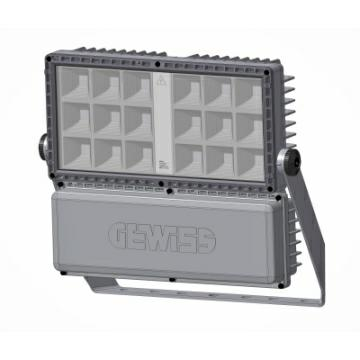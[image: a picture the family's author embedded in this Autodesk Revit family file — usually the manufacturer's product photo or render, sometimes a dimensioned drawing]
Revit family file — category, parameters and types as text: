
# Revit family: Lighting-Proiezione-GEWISS-SMART[PRO]2.0-PROIETTORI-LED-MEDIA-POTENZA_1MODULI_DALI_CLI
name_source: partatom
category: Apparecchi per illuminazione
units: mm (PartAtom-declared; Revit-internal decimal feet)

## family parameters
Condiviso = No
Host = Superficie
Punto di calcolo locali = Sì
Quota connettore circolare = Usa diametro
Sorgente d'illuminazione = No
Taglio con vuoti quando caricato = No
Tipo di parte = Normale

## types (1)
- Lighting-Proiezione-GEWISS-SMART[PRO]2.0-PROIETTORI-LED-MEDIA-POTENZA_1MODULI_DALI_CLI
    Alimentatore = Incluso
    Apparecchio a ridotta temperatura superficiale = Si
    Applicazione = Interno / Esterno
    Cablaggio = Connettore stagno
    Caratteristiche elettriche e gestione della luce = -
    Caratteristiche ottiche e illuminotecniche = -
    Catalogo = LIGHTING
    Certificazione DIN 18032-3 = Si
    Certificazioni e classificazioni = -
    Classe fotobiologica = -
    Classe isolamento = I
    Classificazione: = -
    Codice digitale univoco (Datamatrix) = Attualmente non presente
    Colore = Grigio grafite
    Contesto = Illuminazione di grandi aree, impianti sportivi
    Controllo abbagliamento e luminanza = G*6 - ULOR = 0
    Corpo = Alluminio pressofuso
    Descrizione = SMARTPRO2.0 1M 5700K CRI80 A3 DALI CL1
    Dispositivo di protezione = DM 6 kV / CM 10 kV
    Durata di vita = L90B10 (Tq+25°C) - 50000h L90B10 (Tq+50°C) = 32000h L80B10 (Tq+25°C) - 110000h
    Efficienza luminosa (lm/W) = 107
    Finitura colore = Verniciato a polvere poliestere
    Fissaggio = Staffa
    Frequenza nominale (Hz) = 50 / 60
    GW - Codice Electrocod = 2424
    Gancio di chiusura = Viti metriche esagonali
    Garanzia = 5 anni
    Grado di protezione = IP66
    Gruppo ottico = Parabola in alluminio anodizzato brillantato con alluminio puro 99,99%
    Guarnizioni = silicone antinvecchiamento
    IDF = 3db2d485-13a8-481c-aaf0-cc777464d260
    IDT = 706d4f98386b454aa472bb2581cb3bfe
    IPEA = STRADALE = A // GRANDI AREE = A3+ // CICLOPEDONALI = A+ // AREE VERDI = A+ // CENTRO STORICO = A5+ // ALTRO = A5+
    Immagine tipo = SMARTPRO20_1M.jpg
    Inclinazione = Rotazione su staffa con goniometro integrato
    Indice di resa cromatica = CRI-80
    Informazioni generali = -
    Installazione e manutenzione = -
    Lumen output (lm) = 17600
    Materiali = -
    Modello = GWP2185ND
    Norma di riferimento = EN60598-1; EN60598-2-5; EN60598-2-24; IEC 62778; IEC62471; EN13201
    Ottica = A3 - Asimmetrica Stretta
    Peso (kg): = 5,7
    Potenza di sistema = 165W
    Produttore = GEWISS S.p.A.
    Prospetto di default = 1219 mm
    Resistenza agli urti = IK08
    Resistenza al filo incandescente = -
    SEO = Proiettore
    Scheda Tecnica = https://www.gewiss.com
    Schermo = Vetro piano extrachiaro spessore 4mm
    Sistema di controllo = DALI
    Sostituibilità gruppo ottico = Non disponibile
    Sostituibilità piastra di cablaggio = Non disponibile
    Superficie massima esposta al vento : = 0,085 m2
    Temperatura di colore = 5700K
    Temperatura di esercizio = -30 +50 °C
    Temperatura di stoccaggio = -
    Tensione di alimentazione = 220 - 240 V
    Tipo di apparecchio = Apparecchio per proiezione LED di piccola, media e alta potenza
    Tipo di installazione e montaggio = Torrefaro - Parete - Terra
    Tipologia sorgente luminosa = LED - Non sostituibile
    Tolleranza cromatica = SDCM = 3
    URL = https://www.gewiss.com
    Vano di alimentazione = Integrato
    Versione file RFA = 20.11
    Versioni = Luce fredda 5700K
    Viti esterne = Acciaio inossidabile
